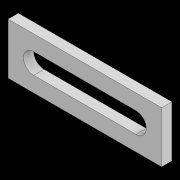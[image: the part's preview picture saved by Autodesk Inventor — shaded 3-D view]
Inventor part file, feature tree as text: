
AUTODESK INVENTOR PART (.ipt)
format: ipt  version: 2021 (Build 250183000, 183)  size: 87,552 bytes
history: native  units: in
note: dims shown in document units (in); Inventor stores cm internally (conversion verified against a paired STEP export)
features: extrude x1, sketch x1
ambient origin geometry x8: Origin, YZ Plane, XZ Plane, XY Plane, X Axis, Y Axis, Z Axis, Center Point
bodies: Solid1 (feature_tree)
feature tree (2):
  extrude  "Extrusion1"  Depth=0.7874in
  sketch  "Sketch1"  dims[d0=2.3622in d1=0.7874in d2=0.315in d3=1.5748in d5=0.1575in d6=0.0in]
